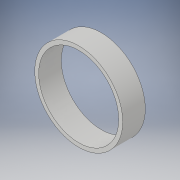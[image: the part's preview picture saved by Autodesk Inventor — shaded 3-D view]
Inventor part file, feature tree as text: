
AUTODESK INVENTOR PART (.ipt)
format: ipt  version: 2019 (Build 230136000, 136)  size: 103,936 bytes
history: native  units: mm
features: extrude x2, sketch x2
ambient origin geometry x8: Origin, YZ Plane, XZ Plane, XY Plane, X Axis, Y Axis, Z Axis, Center Point
bodies: Solid1 (feature_tree)
feature tree (4):
  extrude  "Extrusion1"  Depth=1.82mm TaperAngle=0.0deg
  extrude  "Extrusion2"  Depth=1.82mm TaperAngle=0.0deg
  sketch  "Sketch1"  dims[d0=7.1mm d1=1.82mm d2=0.0mm]
  sketch  "Sketch2"  dims[d3=6.46mm d4=1.82mm d5=0.0mm]
